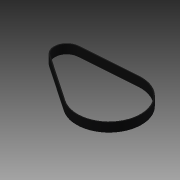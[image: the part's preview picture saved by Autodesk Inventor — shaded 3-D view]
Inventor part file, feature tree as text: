
AUTODESK INVENTOR PART (.ipt)
format: ipt  version: 2014 SP1 (Build 180222100, 222)  size: 109,056 bytes
history: native  units: in
note: dims shown in document units (in); Inventor stores cm internally (conversion verified against a paired STEP export)
features: other x1, extrude x1, sketch x1
ambient origin geometry x8: Origin, YZ Plane, XZ Plane, XY Plane, X Axis, Y Axis, Z Axis, Center Point
bodies: Solid1 (feature_tree)
feature tree (3):
  other  "mountsketch_alt.ipt"
  extrude  "Extrusion1"  TaperAngle=360.0deg  [1 undecoded]
  sketch  "Sketch1"  dims[d0=0.3937in d2=0.8661in d3=0.1693in d5=0.8661in d6=2.5984in d7=2.4577in d13=1.5748in d17=2.454in d18=1.9042in d15=360.0deg d1=2.5063in d4=0.9398in d8=2.4577in d11=0.3543in d12=0.0in]
note: 1 required parameter value undecoded (feature->parameter linkage not recoverable at this tier; creation-order binding heuristic only, values carry confidence <= 0.55)
